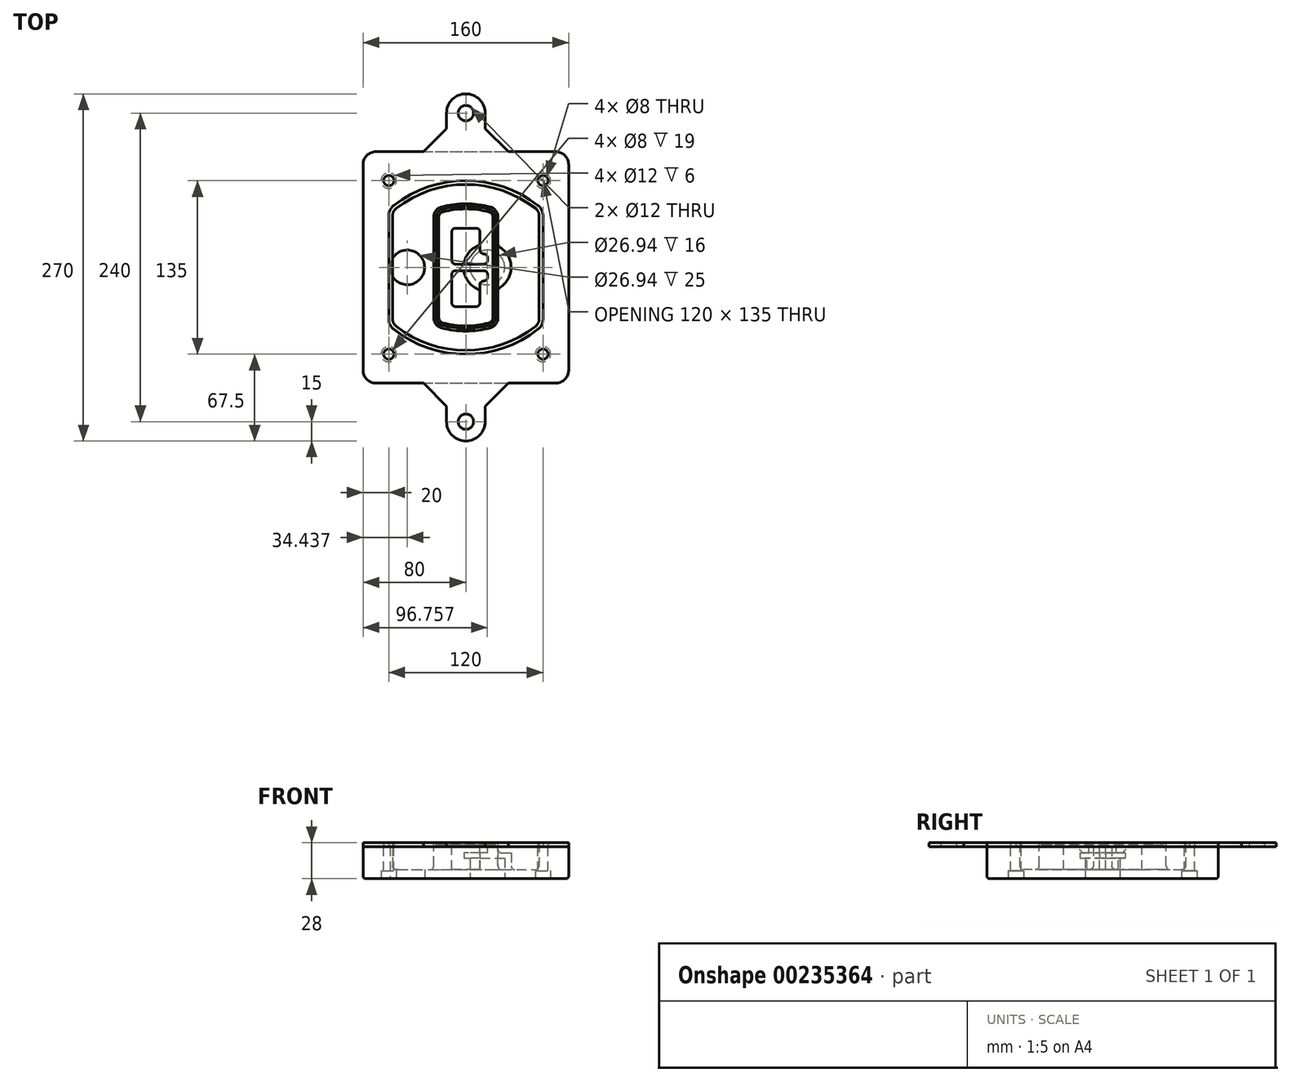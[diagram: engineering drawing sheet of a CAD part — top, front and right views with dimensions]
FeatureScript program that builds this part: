
annotation { "Feature Type Name" : "Feature", "Feature Type Description" : "" }
export const myFeature = defineFeature(function(context is Context, id is Id, definition is map)
    precondition{}
    {
        {
            var Q0;
            Q0=qCreatedBy(makeId("Top.planeOp"),FACE);
            var sketch = newSketch(context, id + "F0", { "sketchPlane" : qUnion([Q0])});
            skPoint(sketch, "E0.rect.middle", {"position": v(0, 0) * mm});
            skLineSegment(sketch, "E1.bottom", {"start": v(-70, -90) * mm, "end": v(70, -90) * mm});
            skLineSegment(sketch, "E1.top", {"start": v(-70, 90) * mm, "end": v(70, 90) * mm});
            skLineSegment(sketch, "E1.left", {"start": v(-80, -80) * mm, "end": v(-80, 80) * mm});
            skLineSegment(sketch, "E1.right", {"start": v(80, -80) * mm, "end": v(80, 80) * mm});
            skLineSegment(sketch, "E2", {"start": v(-80, 90) * mm, "end": v(80, -90) * mm, "construction": true});
            skLineSegment(sketch, "E3", {"start": v(80, 90) * mm, "end": v(-80, -90) * mm, "construction": true});
            skCircle(sketch, "E4", {"center": v(-60, 67.5) * mm, "radius": 4 * mm});
            skCircle(sketch, "E5", {"center": v(60, 67.5) * mm, "radius": 4 * mm});
            skCircle(sketch, "E6", {"center": v(60, -67.5) * mm, "radius": 4 * mm});
            skCircle(sketch, "E7", {"center": v(-60, -67.5) * mm, "radius": 4 * mm});
            skLineSegment(sketch, "E8", {"start": v(-60, 67.5) * mm, "end": v(60, 67.5) * mm, "construction": true});
            skLineSegment(sketch, "E9", {"start": v(60, 67.5) * mm, "end": v(60, -67.5) * mm, "construction": true});
            skLineSegment(sketch, "E10", {"start": v(60, -67.5) * mm, "end": v(-60, -67.5) * mm, "construction": true});
            skLineSegment(sketch, "E11", {"start": v(-60, -67.5) * mm, "end": v(-60, 67.5) * mm, "construction": true});
            skLineSegment(sketch, "E12", {"start": v(-60, 40.3) * mm, "end": v(-60, -40.3) * mm});
            skLineSegment(sketch, "E13", {"start": v(60, 40.3) * mm, "end": v(60, -40.3) * mm});
            skArc(sketch, "E14", {"start": v(56.15, 48.18) * mm, "mid": v(0, 67.5) * mm, "end": v(-56.15, 48.18) * mm});
            skArc(sketch, "E15", {"start": v(-56.15, -48.18) * mm, "mid": v(0, -67.5) * mm, "end": v(56.15, -48.18) * mm});
            skLineSegment(sketch, "E16", {"start": v(-60, 0) * mm, "end": v(60, 0) * mm, "construction": true});
            skPoint(sketch, "E17.visualSharp", {"position": v(-60, -45) * mm});
            skArc(sketch, "E17.filletArc", {"start": v(-60, -40.3) * mm, "mid": v(-58.99, -44.68) * mm, "end": v(-56.15, -48.18) * mm});
            skPoint(sketch, "E18.visualSharp", {"position": v(-60, 45) * mm});
            skArc(sketch, "E18.filletArc", {"start": v(-56.15, 48.18) * mm, "mid": v(-58.99, 44.68) * mm, "end": v(-60, 40.3) * mm});
            skPoint(sketch, "E19.visualSharp", {"position": v(60, 45) * mm});
            skArc(sketch, "E19.filletArc", {"start": v(60, 40.3) * mm, "mid": v(58.99, 44.68) * mm, "end": v(56.15, 48.18) * mm});
            skPoint(sketch, "E20.visualSharp", {"position": v(60, -45) * mm});
            skArc(sketch, "E20.filletArc", {"start": v(56.15, -48.18) * mm, "mid": v(58.99, -44.68) * mm, "end": v(60, -40.3) * mm});
            skPoint(sketch, "E21.visualSharp", {"position": v(-80, 90) * mm});
            skArc(sketch, "E21.filletArc", {"start": v(-70, 90) * mm, "mid": v(-77.07, 87.07) * mm, "end": v(-80, 80) * mm});
            skPoint(sketch, "E22.visualSharp", {"position": v(80, 90) * mm});
            skArc(sketch, "E22.filletArc", {"start": v(80, 80) * mm, "mid": v(77.07, 87.07) * mm, "end": v(70, 90) * mm});
            skPoint(sketch, "E23.visualSharp", {"position": v(80, -90) * mm});
            skArc(sketch, "E23.filletArc", {"start": v(70, -90) * mm, "mid": v(77.07, -87.07) * mm, "end": v(80, -80) * mm});
            skPoint(sketch, "E24.visualSharp", {"position": v(-80, -90) * mm});
            skArc(sketch, "E24.filletArc", {"start": v(-80, -80) * mm, "mid": v(-77.07, -87.07) * mm, "end": v(-70, -90) * mm});
            skArc(sketch, "E25.0", {"start": v(57, 40.3) * mm, "mid": v(56.3, 43.36) * mm, "end": v(54.3, 45.81) * mm});
            skLineSegment(sketch, "E25.1", {"start": v(57, 40.3) * mm, "end": v(57, -40.3) * mm});
            skArc(sketch, "E25.2", {"start": v(54.3, -45.81) * mm, "mid": v(56.3, -43.36) * mm, "end": v(57, -40.3) * mm});
            skArc(sketch, "E25.3", {"start": v(-54.3, -45.81) * mm, "mid": v(0, -64.5) * mm, "end": v(54.3, -45.81) * mm});
            skArc(sketch, "E25.4", {"start": v(-57, -40.3) * mm, "mid": v(-56.3, -43.36) * mm, "end": v(-54.3, -45.81) * mm});
            skArc(sketch, "E25.5", {"start": v(54.3, 45.81) * mm, "mid": v(0, 64.5) * mm, "end": v(-54.3, 45.81) * mm});
            skLineSegment(sketch, "E25.6", {"start": v(-57, 40.3) * mm, "end": v(-57, -40.3) * mm});
            skArc(sketch, "E25.7", {"start": v(-54.3, 45.81) * mm, "mid": v(-56.3, 43.36) * mm, "end": v(-57, 40.3) * mm});
            skArc(sketch, "E26.0", {"start": v(-58.62, 51.33) * mm, "mid": v(-62.58, 46.43) * mm, "end": v(-64, 40.3) * mm});
            skArc(sketch, "E26.1", {"start": v(58.62, 51.33) * mm, "mid": v(0, 71.5) * mm, "end": v(-58.62, 51.33) * mm});
            skArc(sketch, "E26.2", {"start": v(64, 40.3) * mm, "mid": v(62.58, 46.43) * mm, "end": v(58.62, 51.33) * mm});
            skLineSegment(sketch, "E26.3", {"start": v(64, 40.3) * mm, "end": v(64, -40.3) * mm});
            skArc(sketch, "E26.4", {"start": v(58.62, -51.33) * mm, "mid": v(62.58, -46.43) * mm, "end": v(64, -40.3) * mm});
            skLineSegment(sketch, "E26.5", {"start": v(-64, 40.3) * mm, "end": v(-64, -40.3) * mm});
            skArc(sketch, "E26.6", {"start": v(-58.62, -51.33) * mm, "mid": v(0, -71.5) * mm, "end": v(58.62, -51.33) * mm});
            skArc(sketch, "E26.7", {"start": v(-64, -40.3) * mm, "mid": v(-62.58, -46.43) * mm, "end": v(-58.62, -51.33) * mm});
            skSolve(sketch);
        }
        {
            var Q0;
            Q0=makeQuery(id+"F0.imprint","IMPRINT",FACE,{"disambiguationData":[TD([[makeQuery(id+"F0.imprint","IMPRINT",EDGE,{"derivedFrom":sQuery(id+"F0.wireOp",EDGE,"E1.bottom")}),1.0]])]});
            var Q1;
            Q1=makeQuery(id+"F0.imprint","IMPRINT",FACE,{"disambiguationData":[TD([[makeQuery(id+"F0.imprint","IMPRINT",EDGE,{"derivedFrom":sQuery(id+"F0.wireOp",EDGE,"E12")}),1.0]])]});
            var Q2;
            Q2=makeQuery(id+"F0.imprint","IMPRINT",FACE,{"disambiguationData":[TD([[makeQuery(id+"F0.imprint","IMPRINT",EDGE,{"derivedFrom":sQuery(id+"F0.wireOp",EDGE,"E25.0")}),1.0]])]});
            var Q3;
            Q3=makeQuery(id+"F0.imprint","IMPRINT",FACE,{"disambiguationData":[TD([[makeQuery(id+"F0.imprint","IMPRINT",EDGE,{"derivedFrom":sQuery(id+"F0.wireOp",EDGE,"E12")}),-1.0]])]});
            extrude(context, id + "F1", {"entities" : qUnion([Q0, Q1, Q2, Q3]), "oppositeDirection" : true, "depth" : 25 * mm});
        }
        {
            var Q0;
            Q0=makeQuery(id+"F0.imprint","IMPRINT",FACE,{"disambiguationData":[TD([[makeQuery(id+"F0.imprint","IMPRINT",EDGE,{"derivedFrom":sQuery(id+"F0.wireOp",EDGE,"E12")}),1.0]])]});
            extrude(context, id + "F2", {"entities" : qUnion([Q0]), "operationType" : NewBodyOperationType.ADD, "depth" : 3 * mm});
        }
        {
            var Q0;
            Q0=makeQuery(id+"F0.imprint","IMPRINT",FACE,{"disambiguationData":[TD([[makeQuery(id+"F0.imprint","IMPRINT",EDGE,{"derivedFrom":sQuery(id+"F0.wireOp",EDGE,"E25.0")}),1.0]])]});
            extrude(context, id + "F3", {"entities" : qUnion([Q0]), "operationType" : NewBodyOperationType.REMOVE, "oppositeDirection" : true, "depth" : 18 * mm});
        }
        {
            var Q0;
            Q0=makeQuery(id+"F2.opExtrude","CAP_FACE",FACE,{"disambiguationData":[OSD([sQuery(id+"F0.wireOp",EDGE,"E12"),sQuery(id+"F0.wireOp",EDGE,"E13"),sQuery(id+"F0.wireOp",EDGE,"E14"),sQuery(id+"F0.wireOp",EDGE,"E15"),sQuery(id+"F0.wireOp",EDGE,"E17.filletArc"),sQuery(id+"F0.wireOp",EDGE,"E18.filletArc"),sQuery(id+"F0.wireOp",EDGE,"E19.filletArc"),sQuery(id+"F0.wireOp",EDGE,"E20.filletArc"),sQuery(id+"F0.wireOp",EDGE,"E25.0"),sQuery(id+"F0.wireOp",EDGE,"E25.1"),sQuery(id+"F0.wireOp",EDGE,"E25.2"),sQuery(id+"F0.wireOp",EDGE,"E25.3"),sQuery(id+"F0.wireOp",EDGE,"E25.4"),sQuery(id+"F0.wireOp",EDGE,"E25.5"),sQuery(id+"F0.wireOp",EDGE,"E25.6"),sQuery(id+"F0.wireOp",EDGE,"E25.7")])],"isStart":false});
            var sketch = newSketch(context, id + "F4", { "sketchPlane" : qUnion([Q0])});
            skArc(sketch, "E27.0", {"start": v(-19.08, -46.97) * mm, "mid": v(0, -49.5) * mm, "end": v(19.08, -46.97) * mm});
            skArc(sketch, "E28.0", {"start": v(19.08, 46.97) * mm, "mid": v(0, 49.5) * mm, "end": v(-19.08, 46.97) * mm});
            skLineSegment(sketch, "E29", {"start": v(-25, 39.25) * mm, "end": v(-25, -39.25) * mm});
            skLineSegment(sketch, "E30", {"start": v(25, 39.25) * mm, "end": v(25, -39.25) * mm});
            skLineSegment(sketch, "E31", {"start": v(-25, 45.1) * mm, "end": v(25, 45.1) * mm, "construction": true});
            skLineSegment(sketch, "E32", {"start": v(-25, -45.1) * mm, "end": v(25, -45.1) * mm, "construction": true});
            skPoint(sketch, "E33.visualSharp", {"position": v(-25, 45.1) * mm});
            skArc(sketch, "E33.filletArc", {"start": v(-19.08, 46.97) * mm, "mid": v(-23.35, 44.11) * mm, "end": v(-25, 39.25) * mm});
            skPoint(sketch, "E34.visualSharp", {"position": v(25, 45.1) * mm});
            skArc(sketch, "E34.filletArc", {"start": v(25, 39.25) * mm, "mid": v(23.35, 44.11) * mm, "end": v(19.08, 46.97) * mm});
            skPoint(sketch, "E35.visualSharp", {"position": v(25, -45.1) * mm});
            skArc(sketch, "E35.filletArc", {"start": v(19.08, -46.97) * mm, "mid": v(23.35, -44.11) * mm, "end": v(25, -39.25) * mm});
            skPoint(sketch, "E36.visualSharp", {"position": v(-25, -45.1) * mm});
            skArc(sketch, "E36.filletArc", {"start": v(-25, -39.25) * mm, "mid": v(-23.35, -44.11) * mm, "end": v(-19.08, -46.97) * mm});
            skArc(sketch, "E37.0", {"start": v(54.3, 45.81) * mm, "mid": v(0, 64.5) * mm, "end": v(-54.3, 45.81) * mm});
            skArc(sketch, "E37.1", {"start": v(-54.3, 45.81) * mm, "mid": v(-56.3, 43.36) * mm, "end": v(-57, 40.3) * mm});
            skLineSegment(sketch, "E37.2", {"start": v(-57, 40.3) * mm, "end": v(-57, -40.3) * mm});
            skArc(sketch, "E37.3", {"start": v(-57, -40.3) * mm, "mid": v(-56.3, -43.36) * mm, "end": v(-54.3, -45.81) * mm});
            skArc(sketch, "E37.4", {"start": v(-54.3, -45.81) * mm, "mid": v(0, -64.5) * mm, "end": v(54.3, -45.81) * mm});
            skArc(sketch, "E37.5", {"start": v(54.3, -45.81) * mm, "mid": v(56.3, -43.36) * mm, "end": v(57, -40.3) * mm});
            skLineSegment(sketch, "E37.6", {"start": v(57, 40.3) * mm, "end": v(57, -40.3) * mm});
            skArc(sketch, "E37.7", {"start": v(57, 40.3) * mm, "mid": v(56.3, 43.36) * mm, "end": v(54.3, 45.81) * mm});
            skLineSegment(sketch, "E38.0", {"start": v(23, 39.25) * mm, "end": v(23, -39.25) * mm});
            skArc(sketch, "E38.1", {"start": v(18.56, -45.04) * mm, "mid": v(21.76, -42.9) * mm, "end": v(23, -39.25) * mm});
            skArc(sketch, "E38.2", {"start": v(-18.56, -45.04) * mm, "mid": v(0, -47.5) * mm, "end": v(18.56, -45.04) * mm});
            skArc(sketch, "E38.3", {"start": v(-23, -39.25) * mm, "mid": v(-21.76, -42.9) * mm, "end": v(-18.56, -45.04) * mm});
            skLineSegment(sketch, "E38.4", {"start": v(-23, 39.25) * mm, "end": v(-23, -39.25) * mm});
            skArc(sketch, "E38.5", {"start": v(23, 39.25) * mm, "mid": v(21.76, 42.9) * mm, "end": v(18.56, 45.04) * mm});
            skArc(sketch, "E38.6", {"start": v(-18.56, 45.04) * mm, "mid": v(-21.76, 42.9) * mm, "end": v(-23, 39.25) * mm});
            skArc(sketch, "E38.7", {"start": v(18.56, 45.04) * mm, "mid": v(0, 47.5) * mm, "end": v(-18.56, 45.04) * mm});
            skArc(sketch, "E39.0", {"start": v(21, 39.25) * mm, "mid": v(20.18, 41.68) * mm, "end": v(18.04, 43.1) * mm});
            skLineSegment(sketch, "E39.1", {"start": v(21, 39.25) * mm, "end": v(21, -39.25) * mm});
            skArc(sketch, "E39.2", {"start": v(18.04, -43.1) * mm, "mid": v(20.18, -41.68) * mm, "end": v(21, -39.25) * mm});
            skArc(sketch, "E39.3", {"start": v(-18.04, -43.1) * mm, "mid": v(0, -45.5) * mm, "end": v(18.04, -43.1) * mm});
            skArc(sketch, "E39.4", {"start": v(-21, -39.25) * mm, "mid": v(-20.18, -41.68) * mm, "end": v(-18.04, -43.1) * mm});
            skArc(sketch, "E39.5", {"start": v(18.04, 43.1) * mm, "mid": v(0, 45.5) * mm, "end": v(-18.04, 43.1) * mm});
            skLineSegment(sketch, "E39.6", {"start": v(-21, 39.25) * mm, "end": v(-21, -39.25) * mm});
            skArc(sketch, "E39.7", {"start": v(-18.04, 43.1) * mm, "mid": v(-20.18, 41.68) * mm, "end": v(-21, 39.25) * mm});
            skLineSegment(sketch, "E40", {"start": v(-25, 0) * mm, "end": v(25, 0) * mm, "construction": true});
            skLineSegment(sketch, "E41", {"start": v(-11, 5.5) * mm, "end": v(-11, 27.5) * mm});
            skLineSegment(sketch, "E42", {"start": v(-8, 30.5) * mm, "end": v(8, 30.5) * mm});
            skLineSegment(sketch, "E43", {"start": v(11, 27.5) * mm, "end": v(11, 13.5) * mm});
            skLineSegment(sketch, "E44", {"start": v(14, 10.5) * mm, "end": v(14, 10.5) * mm});
            skLineSegment(sketch, "E45", {"start": v(17, 7.5) * mm, "end": v(17, 5.5) * mm});
            skLineSegment(sketch, "E46", {"start": v(14, 2.5) * mm, "end": v(-8, 2.5) * mm});
            skPoint(sketch, "E47.visualSharp", {"position": v(-11, 30.5) * mm});
            skArc(sketch, "E47.filletArc", {"start": v(-8, 30.5) * mm, "mid": v(-10.12, 29.62) * mm, "end": v(-11, 27.5) * mm});
            skPoint(sketch, "E48.visualSharp", {"position": v(11, 30.5) * mm});
            skArc(sketch, "E48.filletArc", {"start": v(11, 27.5) * mm, "mid": v(10.12, 29.62) * mm, "end": v(8, 30.5) * mm});
            skPoint(sketch, "E49.visualSharp", {"position": v(11, 10.5) * mm});
            skArc(sketch, "E49.filletArc", {"start": v(11, 13.5) * mm, "mid": v(11.88, 11.38) * mm, "end": v(14, 10.5) * mm});
            skPoint(sketch, "E50.visualSharp", {"position": v(17, 10.5) * mm});
            skArc(sketch, "E50.filletArc", {"start": v(17, 7.5) * mm, "mid": v(16.12, 9.62) * mm, "end": v(14, 10.5) * mm});
            skPoint(sketch, "E51.visualSharp", {"position": v(17, 2.5) * mm});
            skArc(sketch, "E51.filletArc", {"start": v(14, 2.5) * mm, "mid": v(16.12, 3.38) * mm, "end": v(17, 5.5) * mm});
            skPoint(sketch, "E52.visualSharp", {"position": v(-11, 2.5) * mm});
            skArc(sketch, "E52.filletArc", {"start": v(-11, 5.5) * mm, "mid": v(-10.12, 3.38) * mm, "end": v(-8, 2.5) * mm});
            skLineSegment(sketch, "E53.0.MirrorCS", {"start": v(14, -2.5) * mm, "end": v(-8, -2.5) * mm});
            skArc(sketch, "E54.0.MirrorCS", {"start": v(-11, -5.5) * mm, "mid": v(-10.12, -3.38) * mm, "end": v(-8, -2.5) * mm});
            skLineSegment(sketch, "E55.0.MirrorCS", {"start": v(-11, -5.5) * mm, "end": v(-11, -27.5) * mm});
            skArc(sketch, "E56.0.MirrorCS", {"start": v(-8, -30.5) * mm, "mid": v(-10.12, -29.62) * mm, "end": v(-11, -27.5) * mm});
            skLineSegment(sketch, "E57.0.MirrorCS", {"start": v(-8, -30.5) * mm, "end": v(8, -30.5) * mm});
            skArc(sketch, "E58.0.MirrorCS", {"start": v(11, -27.5) * mm, "mid": v(10.12, -29.62) * mm, "end": v(8, -30.5) * mm});
            skLineSegment(sketch, "E59.0.MirrorCS", {"start": v(11, -27.5) * mm, "end": v(11, -13.5) * mm});
            skArc(sketch, "E60.0.MirrorCS", {"start": v(11, -13.5) * mm, "mid": v(11.88, -11.38) * mm, "end": v(14, -10.5) * mm});
            skArc(sketch, "E61.0.MirrorCS", {"start": v(17, -7.5) * mm, "mid": v(16.12, -9.62) * mm, "end": v(14, -10.5) * mm});
            skLineSegment(sketch, "E62.0.MirrorCS", {"start": v(17, -7.5) * mm, "end": v(17, -5.5) * mm});
            skArc(sketch, "E63.0.MirrorCS", {"start": v(14, -2.5) * mm, "mid": v(16.12, -3.38) * mm, "end": v(17, -5.5) * mm});
            skSolve(sketch);
        }
        {
            var Q0;
            Q0=makeQuery(id+"F4.imprint","IMPRINT",FACE,{"disambiguationData":[TD([[makeQuery(id+"F4.imprint","IMPRINT",EDGE,{"derivedFrom":sQuery(id+"F4.wireOp",EDGE,"E27.0")}),1.0]])]});
            var Q1;
            Q1=makeQuery(id+"F4.imprint","IMPRINT",FACE,{"disambiguationData":[TD([[makeQuery(id+"F4.imprint","IMPRINT",EDGE,{"derivedFrom":sQuery(id+"F4.wireOp",EDGE,"E38.0")}),-1.0]])]});
            var Q2;
            Q2=makeQuery(id+"F4.imprint","IMPRINT",FACE,{"disambiguationData":[TD([[makeQuery(id+"F4.imprint","IMPRINT",EDGE,{"derivedFrom":sQuery(id+"F4.wireOp",EDGE,"E39.0")}),1.0]])]});
            extrude(context, id + "F5", {"entities" : qUnion([Q0, Q1, Q2]), "operationType" : NewBodyOperationType.ADD, "endBound" : BoundingType.UP_TO_NEXT, "oppositeDirection" : true, "depth" : 25 * mm});
        }
        {
            var Q0;
            Q0=makeQuery(id+"F4.imprint","IMPRINT",FACE,{"disambiguationData":[TD([[makeQuery(id+"F4.imprint","IMPRINT",EDGE,{"derivedFrom":sQuery(id+"F4.wireOp",EDGE,"E38.0")}),-1.0]])]});
            extrude(context, id + "F6", {"entities" : qUnion([Q0]), "operationType" : NewBodyOperationType.REMOVE, "oppositeDirection" : true, "depth" : 2 * mm});
        }
        {
            var Q0;
            Q0=makeQuery(id+"F1.opExtrude","CAP_FACE",FACE,{"disambiguationData":[OSD([sQuery(id+"F0.wireOp",EDGE,"E1.bottom"),sQuery(id+"F0.wireOp",EDGE,"E1.top"),sQuery(id+"F0.wireOp",EDGE,"E1.left"),sQuery(id+"F0.wireOp",EDGE,"E1.right"),sQuery(id+"F0.wireOp",EDGE,"E4"),sQuery(id+"F0.wireOp",EDGE,"E5"),sQuery(id+"F0.wireOp",EDGE,"E6"),sQuery(id+"F0.wireOp",EDGE,"E7"),sQuery(id+"F0.wireOp",EDGE,"E21.filletArc"),sQuery(id+"F0.wireOp",EDGE,"E22.filletArc"),sQuery(id+"F0.wireOp",EDGE,"E23.filletArc"),sQuery(id+"F0.wireOp",EDGE,"E24.filletArc")])],"isStart":false});
            var sketch = newSketch(context, id + "F7", { "sketchPlane" : qUnion([Q0])});
            skCircle(sketch, "E64", {"center": v(16.76, 0) * mm, "radius": 13.47 * mm});
            skCircle(sketch, "E65", {"center": v(-45.56, 0) * mm, "radius": 13.47 * mm});
            skLineSegment(sketch, "E66", {"start": v(80, 0) * mm, "end": v(-80, 0) * mm});
            skCircle(sketch, "E67", {"center": v(16.76, 0) * mm, "radius": 18.47 * mm});
            skCircle(sketch, "E68", {"center": v(60, -67.5) * mm, "radius": 6 * mm});
            skCircle(sketch, "E69", {"center": v(-60, -67.5) * mm, "radius": 6 * mm});
            skCircle(sketch, "E70", {"center": v(-60, 67.5) * mm, "radius": 6 * mm});
            skCircle(sketch, "E71", {"center": v(60, 67.5) * mm, "radius": 6 * mm});
            skSolve(sketch);
        }
        {
            var Q0;
            {var subQ1=sQuery(id+"F7.wireOp",EDGE,"E66");var subQ4=sQuery(id+"F7.wireOp",EDGE,"E64");var subQ6=makeQuery(id+"F7.imprint","INTERSECT",VERTEX,{"disambiguationData":[OD(0.0)],"derivedFrom":[subQ4,subQ1]});Q0=makeQuery(id+"F7.imprint","IMPRINT",FACE,{"disambiguationData":[TD([[makeQuery(id+"F7.imprint","IMPRINT",EDGE,{"disambiguationData":[TD([[subQ6,-1.0]])],"derivedFrom":subQ4}),-1.0]])]});}
            var Q1;
            {var subQ0=sQuery(id+"F7.wireOp",EDGE,"E66");var subQ1=sQuery(id+"F7.wireOp",EDGE,"E64");var subQ3=makeQuery(id+"F7.imprint","INTERSECT",VERTEX,{"disambiguationData":[OD(0.0)],"derivedFrom":[subQ1,subQ0]});Q1=makeQuery(id+"F7.imprint","IMPRINT",FACE,{"disambiguationData":[TD([[makeQuery(id+"F7.imprint","IMPRINT",EDGE,{"disambiguationData":[TD([[subQ3,-1.0]])],"derivedFrom":subQ1}),1.0]])]});}
            var Q2;
            {var subQ0=sQuery(id+"F7.wireOp",EDGE,"E66");var subQ1=sQuery(id+"F7.wireOp",EDGE,"E64");var subQ3=makeQuery(id+"F7.imprint","INTERSECT",VERTEX,{"disambiguationData":[OD(0.0)],"derivedFrom":[subQ1,subQ0]});Q2=makeQuery(id+"F7.imprint","IMPRINT",FACE,{"disambiguationData":[TD([[makeQuery(id+"F7.imprint","IMPRINT",EDGE,{"disambiguationData":[TD([[subQ3,1.0]])],"derivedFrom":subQ1}),1.0]])]});}
            var Q3;
            {var subQ1=sQuery(id+"F7.wireOp",EDGE,"E66");var subQ4=sQuery(id+"F7.wireOp",EDGE,"E64");var subQ6=makeQuery(id+"F7.imprint","INTERSECT",VERTEX,{"disambiguationData":[OD(0.0)],"derivedFrom":[subQ4,subQ1]});Q3=makeQuery(id+"F7.imprint","IMPRINT",FACE,{"disambiguationData":[TD([[makeQuery(id+"F7.imprint","IMPRINT",EDGE,{"disambiguationData":[TD([[subQ6,1.0]])],"derivedFrom":subQ4}),-1.0]])]});}
            extrude(context, id + "F8", {"entities" : qUnion([Q0, Q1, Q2, Q3]), "operationType" : NewBodyOperationType.ADD, "oppositeDirection" : true, "depth" : 20 * mm});
        }
        {
            var Q0;
            {var subQ0=sQuery(id+"F7.wireOp",EDGE,"E66");var subQ1=sQuery(id+"F7.wireOp",EDGE,"E64");var subQ3=makeQuery(id+"F7.imprint","INTERSECT",VERTEX,{"disambiguationData":[OD(0.0)],"derivedFrom":[subQ1,subQ0]});Q0=makeQuery(id+"F7.imprint","IMPRINT",FACE,{"disambiguationData":[TD([[makeQuery(id+"F7.imprint","IMPRINT",EDGE,{"disambiguationData":[TD([[subQ3,-1.0]])],"derivedFrom":subQ1}),1.0]])]});}
            var Q1;
            {var subQ0=sQuery(id+"F7.wireOp",EDGE,"E66");var subQ1=sQuery(id+"F7.wireOp",EDGE,"E64");var subQ3=makeQuery(id+"F7.imprint","INTERSECT",VERTEX,{"disambiguationData":[OD(0.0)],"derivedFrom":[subQ1,subQ0]});Q1=makeQuery(id+"F7.imprint","IMPRINT",FACE,{"disambiguationData":[TD([[makeQuery(id+"F7.imprint","IMPRINT",EDGE,{"disambiguationData":[TD([[subQ3,1.0]])],"derivedFrom":subQ1}),1.0]])]});}
            extrude(context, id + "F9", {"entities" : qUnion([Q0, Q1]), "operationType" : NewBodyOperationType.REMOVE, "oppositeDirection" : true, "depth" : 16 * mm});
        }
        {
            var Q0;
            {var subQ0=sQuery(id+"F7.wireOp",EDGE,"E66");var subQ1=sQuery(id+"F7.wireOp",EDGE,"E65");var subQ3=makeQuery(id+"F7.imprint","INTERSECT",VERTEX,{"disambiguationData":[OD(0.0)],"derivedFrom":[subQ1,subQ0]});Q0=makeQuery(id+"F7.imprint","IMPRINT",FACE,{"disambiguationData":[TD([[makeQuery(id+"F7.imprint","IMPRINT",EDGE,{"disambiguationData":[TD([[subQ3,-1.0]])],"derivedFrom":subQ1}),1.0]])]});}
            var Q1;
            {var subQ0=sQuery(id+"F7.wireOp",EDGE,"E66");var subQ1=sQuery(id+"F7.wireOp",EDGE,"E65");var subQ3=makeQuery(id+"F7.imprint","INTERSECT",VERTEX,{"disambiguationData":[OD(0.0)],"derivedFrom":[subQ1,subQ0]});Q1=makeQuery(id+"F7.imprint","IMPRINT",FACE,{"disambiguationData":[TD([[makeQuery(id+"F7.imprint","IMPRINT",EDGE,{"disambiguationData":[TD([[subQ3,1.0]])],"derivedFrom":subQ1}),1.0]])]});}
            extrude(context, id + "F10", {"entities" : qUnion([Q0, Q1]), "operationType" : NewBodyOperationType.REMOVE, "oppositeDirection" : true, "depth" : 25 * mm});
        }
        {
            var Q0;
            Q0=makeQuery(id+"F7.imprint","IMPRINT",FACE,{"disambiguationData":[TD([[makeQuery(id+"F7.imprint","IMPRINT",EDGE,{"derivedFrom":sQuery(id+"F7.wireOp",EDGE,"E68")}),1.0]])]});
            var Q1;
            Q1=makeQuery(id+"F7.imprint","IMPRINT",FACE,{"disambiguationData":[TD([[makeQuery(id+"F7.imprint","IMPRINT",EDGE,{"derivedFrom":makeQuery(id+"F1.opExtrude","CAP_EDGE",EDGE,{"disambiguationData":[OSD([sQuery(id+"F0.wireOp",EDGE,"E5")])],"isStart":false})}),-1.0]])]});
            var Q2;
            Q2=makeQuery(id+"F7.imprint","IMPRINT",FACE,{"disambiguationData":[TD([[makeQuery(id+"F7.imprint","IMPRINT",EDGE,{"derivedFrom":sQuery(id+"F7.wireOp",EDGE,"E69")}),1.0]])]});
            var Q3;
            Q3=makeQuery(id+"F7.imprint","IMPRINT",FACE,{"disambiguationData":[TD([[makeQuery(id+"F7.imprint","IMPRINT",EDGE,{"derivedFrom":makeQuery(id+"F1.opExtrude","CAP_EDGE",EDGE,{"disambiguationData":[OSD([sQuery(id+"F0.wireOp",EDGE,"E4")])],"isStart":false})}),-1.0]])]});
            var Q4;
            Q4=makeQuery(id+"F7.imprint","IMPRINT",FACE,{"disambiguationData":[TD([[makeQuery(id+"F7.imprint","IMPRINT",EDGE,{"derivedFrom":sQuery(id+"F7.wireOp",EDGE,"E70")}),1.0]])]});
            var Q5;
            Q5=makeQuery(id+"F7.imprint","IMPRINT",FACE,{"disambiguationData":[TD([[makeQuery(id+"F7.imprint","IMPRINT",EDGE,{"derivedFrom":makeQuery(id+"F1.opExtrude","CAP_EDGE",EDGE,{"disambiguationData":[OSD([sQuery(id+"F0.wireOp",EDGE,"E7")])],"isStart":false})}),-1.0]])]});
            var Q6;
            Q6=makeQuery(id+"F7.imprint","IMPRINT",FACE,{"disambiguationData":[TD([[makeQuery(id+"F7.imprint","IMPRINT",EDGE,{"derivedFrom":sQuery(id+"F7.wireOp",EDGE,"E71")}),1.0]])]});
            var Q7;
            Q7=makeQuery(id+"F7.imprint","IMPRINT",FACE,{"disambiguationData":[TD([[makeQuery(id+"F7.imprint","IMPRINT",EDGE,{"derivedFrom":makeQuery(id+"F1.opExtrude","CAP_EDGE",EDGE,{"disambiguationData":[OSD([sQuery(id+"F0.wireOp",EDGE,"E6")])],"isStart":false})}),-1.0]])]});
            extrude(context, id + "F11", {"entities" : qUnion([Q0, Q1, Q2, Q3, Q4, Q5, Q6, Q7]), "operationType" : NewBodyOperationType.REMOVE, "oppositeDirection" : true, "depth" : 6 * mm});
        }
        {
            var Q0;
            Q0=makeQuery(id+"F9.boolean.opBoolean","COPY",FACE,{"derivedFrom":makeQuery(id+"F9.opExtrude","CAP_FACE",FACE,{"disambiguationData":[OSD([sQuery(id+"F7.wireOp",EDGE,"E64")])],"isStart":false})});
            var sketch = newSketch(context, id + "F12", { "sketchPlane" : qUnion([Q0])});
            skArc(sketch, "E72.0", {"start": v(11, 17.55) * mm, "mid": v(2.57, 11.82) * mm, "end": v(-1.54, 2.5) * mm});
            skArc(sketch, "E72.1", {"start": v(-1.54, -2.5) * mm, "mid": v(2.57, -11.82) * mm, "end": v(11, -17.55) * mm});
            skLineSegment(sketch, "E73", {"start": v(-1.54, -2.5) * mm, "end": v(14, -2.5) * mm});
            skLineSegment(sketch, "E74.0", {"start": v(14, 2.5) * mm, "end": v(-1.54, 2.5) * mm});
            skArc(sketch, "E74.1", {"start": v(14, 2.5) * mm, "mid": v(16.12, 3.38) * mm, "end": v(17, 5.5) * mm});
            skLineSegment(sketch, "E74.2", {"start": v(17, 7.5) * mm, "end": v(17, 5.5) * mm});
            skArc(sketch, "E74.3", {"start": v(17, 7.5) * mm, "mid": v(16.12, 9.62) * mm, "end": v(14, 10.5) * mm});
            skArc(sketch, "E74.4", {"start": v(11, 13.5) * mm, "mid": v(11.88, 11.38) * mm, "end": v(14, 10.5) * mm});
            skLineSegment(sketch, "E74.5", {"start": v(11, 17.55) * mm, "end": v(11, 13.5) * mm});
            skLineSegment(sketch, "E74.7", {"start": v(14, -2.5) * mm, "end": v(-1.54, -2.5) * mm});
            skArc(sketch, "E74.8", {"start": v(14, -2.5) * mm, "mid": v(16.12, -3.38) * mm, "end": v(17, -5.5) * mm});
            skLineSegment(sketch, "E74.9", {"start": v(17, -7.5) * mm, "end": v(17, -5.5) * mm});
            skArc(sketch, "E74.10", {"start": v(17, -7.5) * mm, "mid": v(16.12, -9.62) * mm, "end": v(14, -10.5) * mm});
            skArc(sketch, "E74.11", {"start": v(11, -13.5) * mm, "mid": v(11.88, -11.38) * mm, "end": v(14, -10.5) * mm});
            skLineSegment(sketch, "E74.12", {"start": v(11, -17.55) * mm, "end": v(11, -13.5) * mm});
            skPoint(sketch, "E75.orphan", {"position": v(11, -27.5) * mm});
            skPoint(sketch, "E76.orphan", {"position": v(-8, -2.5) * mm});
            skPoint(sketch, "E77.orphan", {"position": v(-8, 2.5) * mm});
            skPoint(sketch, "E78.orphan", {"position": v(11, 27.5) * mm});
            skSolve(sketch);
        }
        {
            var Q0;
            {var subQ7=sQuery(id+"F12.wireOp",EDGE,"E72.0");var subQ14=sQuery(id+"F12.wireOp",EDGE,"E72.1");var subQ16=sQuery(id+"F12.wireOp",EDGE,"E74.1");var subQ18=sQuery(id+"F12.wireOp",EDGE,"E74.8");Q0=qUnion([makeQuery(id+"F12.imprint","IMPRINT",FACE,{"disambiguationData":[TD([[makeQuery(id+"F12.imprint","IMPRINT",EDGE,{"derivedFrom":subQ7}),1.0]])]}),makeQuery(id+"F12.imprint","IMPRINT",FACE,{"disambiguationData":[TD([[makeQuery(id+"F12.imprint","IMPRINT",EDGE,{"derivedFrom":subQ14}),1.0]])]}),makeQuery(id+"F12.imprint","IMPRINT",FACE,{"disambiguationData":[TD([[makeQuery(id+"F12.imprint","IMPRINT",EDGE,{"derivedFrom":subQ16}),1.0]])]}),makeQuery(id+"F12.imprint","IMPRINT",FACE,{"disambiguationData":[TD([[makeQuery(id+"F12.imprint","IMPRINT",EDGE,{"derivedFrom":subQ18}),-1.0]])]})]);}
            var Q1;
            Q1=makeQuery(id+"F5.boolean.opBoolean","SPLIT",FACE,{"disambiguationData":[TD([makeQuery(id+"F5.opExtrude","SWEPT_FACE",FACE,{"disambiguationData":[OSD([sQuery(id+"F4.wireOp",EDGE,"E41")])]})])],"derivedFrom":makeQuery(id+"F3.boolean.opBoolean","COPY",FACE,{"derivedFrom":makeQuery(id+"F3.opExtrude","CAP_FACE",FACE,{"disambiguationData":[OSD([sQuery(id+"F0.wireOp",EDGE,"E25.0"),sQuery(id+"F0.wireOp",EDGE,"E25.1"),sQuery(id+"F0.wireOp",EDGE,"E25.2"),sQuery(id+"F0.wireOp",EDGE,"E25.3"),sQuery(id+"F0.wireOp",EDGE,"E25.4"),sQuery(id+"F0.wireOp",EDGE,"E25.5"),sQuery(id+"F0.wireOp",EDGE,"E25.6"),sQuery(id+"F0.wireOp",EDGE,"E25.7")])],"isStart":false})})});
            extrude(context, id + "F13", {"entities" : qUnion([Q0]), "operationType" : NewBodyOperationType.REMOVE, "endBound" : BoundingType.UP_TO_SURFACE, "endBoundEntityFace" : qUnion([Q1]), "depth" : 25 * mm});
        }
        {
            var Q0;
            Q0=makeQuery(id+"F3.boolean.opBoolean","COPY",EDGE,{"derivedFrom":makeQuery(id+"F3.opExtrude","CAP_EDGE",EDGE,{"disambiguationData":[OSD([sQuery(id+"F0.wireOp",EDGE,"E25.6")])],"isStart":false})});
            var Q1;
            Q1=makeQuery(id+"F8.boolean.opBoolean","INTERSECT",EDGE,{"derivedFrom":[makeQuery(id+"F5.opExtrude","SWEPT_FACE",FACE,{"disambiguationData":[OSD([sQuery(id+"F4.wireOp",EDGE,"E30")])]}),makeQuery(id+"F8.opExtrude","CAP_FACE",FACE,{"disambiguationData":[OSD([sQuery(id+"F7.wireOp",EDGE,"E67")])],"isStart":false})]});
            var Q2;
            Q2=makeQuery(id+"F8.boolean.opBoolean","INTERSECT",EDGE,{"disambiguationData":[OD(1.0)],"derivedFrom":[makeQuery(id+"F5.opExtrude","SWEPT_FACE",FACE,{"disambiguationData":[OSD([sQuery(id+"F4.wireOp",EDGE,"E30")])]}),makeQuery(id+"F8.opExtrude","SWEPT_FACE",FACE,{"disambiguationData":[OSD([sQuery(id+"F7.wireOp",EDGE,"E67")])]})]});
            var Q3;
            {var subQ0=sQuery(id+"F4.wireOp",EDGE,"E30");Q3=makeQuery(id+"F8.boolean.opBoolean","SPLIT",EDGE,{"disambiguationData":[TD([makeQuery(id+"F5.opExtrude","SWEPT_FACE",FACE,{"disambiguationData":[OSD([sQuery(id+"F4.wireOp",EDGE,"E35.filletArc")])]})])],"derivedFrom":makeQuery(id+"F5.opExtrude","CAP_EDGE",EDGE,{"disambiguationData":[OSD([subQ0])],"isStart":false})});}
            var Q4;
            {var subQ0=sQuery(id+"F0.wireOp",EDGE,"E25.7");var subQ1=sQuery(id+"F0.wireOp",EDGE,"E25.1");var subQ2=sQuery(id+"F0.wireOp",EDGE,"E25.6");var subQ3=sQuery(id+"F0.wireOp",EDGE,"E25.5");var subQ4=sQuery(id+"F0.wireOp",EDGE,"E25.4");var subQ5=sQuery(id+"F0.wireOp",EDGE,"E25.0");var subQ6=sQuery(id+"F0.wireOp",EDGE,"E25.2");var subQ7=sQuery(id+"F0.wireOp",EDGE,"E25.3");Q4=makeQuery(id+"F8.boolean.opBoolean","INTERSECT",EDGE,{"derivedFrom":[makeQuery(id+"F5.boolean.opBoolean","SPLIT",FACE,{"disambiguationData":[TD([makeQuery(id+"F2.opExtrude","SWEPT_FACE",FACE,{"disambiguationData":[OSD([subQ5])]})])],"derivedFrom":makeQuery(id+"F3.boolean.opBoolean","COPY",FACE,{"derivedFrom":makeQuery(id+"F3.opExtrude","CAP_FACE",FACE,{"disambiguationData":[OSD([subQ5,subQ1,subQ6,subQ7,subQ4,subQ3,subQ2,subQ0])],"isStart":false})})}),makeQuery(id+"F8.opExtrude","SWEPT_FACE",FACE,{"disambiguationData":[OSD([sQuery(id+"F7.wireOp",EDGE,"E67")])]})]});}
            var Q5;
            Q5=makeQuery(id+"F8.boolean.opBoolean","INTERSECT",EDGE,{"disambiguationData":[OD(0.0)],"derivedFrom":[makeQuery(id+"F5.opExtrude","SWEPT_FACE",FACE,{"disambiguationData":[OSD([sQuery(id+"F4.wireOp",EDGE,"E30")])]}),makeQuery(id+"F8.opExtrude","SWEPT_FACE",FACE,{"disambiguationData":[OSD([sQuery(id+"F7.wireOp",EDGE,"E67")])]})]});
            fillet(context, id + "F14", {"entities" : qUnion([Q0, Q1, Q2, Q3, Q4, Q5]), "radius" : 3 * mm, "tangentPropagation" : true, "allowEdgeOverflow" : false});
        }
        {
            var Q0;
            Q0=makeQuery(id+"F1.opExtrude","CAP_EDGE",EDGE,{"disambiguationData":[OSD([sQuery(id+"F0.wireOp",EDGE,"E1.bottom")])],"isStart":false});
            fillet(context, id + "F15", {"entities" : qUnion([Q0]), "radius" : 2 * mm, "tangentPropagation" : true, "allowEdgeOverflow" : false});
        }
        {
            var Q0;
            {var subQ0=sQuery(id+"F0.wireOp",EDGE,"E22.filletArc");var subQ1=sQuery(id+"F0.wireOp",EDGE,"E7");var subQ2=sQuery(id+"F0.wireOp",EDGE,"E6");var subQ3=sQuery(id+"F0.wireOp",EDGE,"E5");var subQ4=sQuery(id+"F0.wireOp",EDGE,"E4");var subQ5=sQuery(id+"F0.wireOp",EDGE,"E1.bottom");var subQ6=sQuery(id+"F0.wireOp",EDGE,"E21.filletArc");var subQ7=sQuery(id+"F0.wireOp",EDGE,"E1.top");var subQ8=sQuery(id+"F0.wireOp",EDGE,"E1.left");var subQ9=sQuery(id+"F0.wireOp",EDGE,"E1.right");var subQ10=sQuery(id+"F0.wireOp",EDGE,"E23.filletArc");var subQ11=sQuery(id+"F0.wireOp",EDGE,"E24.filletArc");Q0=makeQuery(id+"F2.boolean.opBoolean","SPLIT",FACE,{"disambiguationData":[TD([makeQuery(id+"F1.opExtrude","SWEPT_FACE",FACE,{"disambiguationData":[OSD([subQ5])]})])],"derivedFrom":makeQuery(id+"F1.opExtrude","CAP_FACE",FACE,{"disambiguationData":[OSD([subQ5,subQ7,subQ8,subQ9,subQ4,subQ3,subQ2,subQ1,subQ6,subQ0,subQ10,subQ11])],"isStart":true})});}
            var sketch = newSketch(context, id + "F16", { "sketchPlane" : qUnion([Q0])});
            skLineSegment(sketch, "E79.0", {"start": v(60, 40.3) * mm, "end": v(60, -40.3) * mm});
            skArc(sketch, "E79.1", {"start": v(60, 40.3) * mm, "mid": v(58.99, 44.68) * mm, "end": v(56.15, 48.18) * mm});
            skArc(sketch, "E79.2", {"start": v(56.15, 48.18) * mm, "mid": v(0, 67.5) * mm, "end": v(-56.15, 48.18) * mm});
            skArc(sketch, "E79.3", {"start": v(-56.15, 48.18) * mm, "mid": v(-58.99, 44.68) * mm, "end": v(-60, 40.3) * mm});
            skLineSegment(sketch, "E79.4", {"start": v(-60, 40.3) * mm, "end": v(-60, -40.3) * mm});
            skArc(sketch, "E79.5", {"start": v(-60, -40.3) * mm, "mid": v(-58.99, -44.68) * mm, "end": v(-56.15, -48.18) * mm});
            skArc(sketch, "E79.6", {"start": v(-56.15, -48.18) * mm, "mid": v(0, -67.5) * mm, "end": v(56.15, -48.18) * mm});
            skArc(sketch, "E79.7", {"start": v(56.15, -48.18) * mm, "mid": v(58.99, -44.68) * mm, "end": v(60, -40.3) * mm});
            skCircle(sketch, "E79.8", {"center": v(-60, 67.5) * mm, "radius": 4 * mm});
            skCircle(sketch, "E79.9", {"center": v(60, 67.5) * mm, "radius": 4 * mm});
            skCircle(sketch, "E79.10", {"center": v(60, -67.5) * mm, "radius": 4 * mm});
            skCircle(sketch, "E79.11", {"center": v(-60, -67.5) * mm, "radius": 4 * mm});
            skLineSegment(sketch, "E79.12", {"start": v(-80, -80) * mm, "end": v(-80, 80) * mm});
            skArc(sketch, "E79.13", {"start": v(-70, 90) * mm, "mid": v(-77.07, 87.07) * mm, "end": v(-80, 80) * mm});
            skLineSegment(sketch, "E79.14", {"start": v(-70, 90) * mm, "end": v(70, 90) * mm});
            skArc(sketch, "E79.15", {"start": v(80, 80) * mm, "mid": v(77.07, 87.07) * mm, "end": v(70, 90) * mm});
            skLineSegment(sketch, "E79.16", {"start": v(80, -80) * mm, "end": v(80, 80) * mm});
            skArc(sketch, "E79.17", {"start": v(70, -90) * mm, "mid": v(77.07, -87.07) * mm, "end": v(80, -80) * mm});
            skLineSegment(sketch, "E79.18", {"start": v(-70, -90) * mm, "end": v(70, -90) * mm});
            skArc(sketch, "E79.19", {"start": v(-80, -80) * mm, "mid": v(-77.07, -87.07) * mm, "end": v(-70, -90) * mm});
            skLineSegment(sketch, "E80", {"start": v(0, 90) * mm, "end": v(0, 120) * mm, "construction": true});
            skCircle(sketch, "E81", {"center": v(0, 120) * mm, "radius": 6 * mm});
            skLineSegment(sketch, "E82", {"start": v(-33, 90) * mm, "end": v(-15, 108) * mm});
            skLineSegment(sketch, "E83", {"start": v(-15, 108) * mm, "end": v(-15, 120) * mm});
            skLineSegment(sketch, "E84", {"start": v(33, 90) * mm, "end": v(15, 108) * mm});
            skLineSegment(sketch, "E85", {"start": v(15, 108) * mm, "end": v(15, 120) * mm});
            skArc(sketch, "E86", {"start": v(15, 120) * mm, "mid": v(0, 135) * mm, "end": v(-15, 120) * mm});
            skLineSegment(sketch, "E87", {"start": v(-80, 0) * mm, "end": v(80, 0) * mm, "construction": true});
            skLineSegment(sketch, "E88.MirrorCS", {"start": v(15, -108) * mm, "end": v(15, -120) * mm});
            skCircle(sketch, "E89.MirrorC", {"center": v(0, -120) * mm, "radius": 6 * mm});
            skArc(sketch, "E90.MirrorCS", {"start": v(15, -120) * mm, "mid": v(0, -135) * mm, "end": v(-15, -120) * mm});
            skLineSegment(sketch, "E91.MirrorCS", {"start": v(-15, -108) * mm, "end": v(-15, -120) * mm});
            skLineSegment(sketch, "E92.MirrorCS", {"start": v(33, -90) * mm, "end": v(15, -108) * mm});
            skLineSegment(sketch, "E93.MirrorCS", {"start": v(-33, -90) * mm, "end": v(-15, -108) * mm});
            skLineSegment(sketch, "E94.MirrorCS", {"start": v(0, -90) * mm, "end": v(0, -120) * mm, "construction": true});
            skSolve(sketch);
        }
        {
            var Q0;
            Q0 = qSketchRegion(id + "F16", true);
            var Q1;
            Q1=makeQuery(id+"F2.opExtrude","CAP_FACE",FACE,{"disambiguationData":[OSD([sQuery(id+"F0.wireOp",EDGE,"E12"),sQuery(id+"F0.wireOp",EDGE,"E13"),sQuery(id+"F0.wireOp",EDGE,"E14"),sQuery(id+"F0.wireOp",EDGE,"E15"),sQuery(id+"F0.wireOp",EDGE,"E17.filletArc"),sQuery(id+"F0.wireOp",EDGE,"E18.filletArc"),sQuery(id+"F0.wireOp",EDGE,"E19.filletArc"),sQuery(id+"F0.wireOp",EDGE,"E20.filletArc"),sQuery(id+"F0.wireOp",EDGE,"E25.0"),sQuery(id+"F0.wireOp",EDGE,"E25.1"),sQuery(id+"F0.wireOp",EDGE,"E25.2"),sQuery(id+"F0.wireOp",EDGE,"E25.3"),sQuery(id+"F0.wireOp",EDGE,"E25.4"),sQuery(id+"F0.wireOp",EDGE,"E25.5"),sQuery(id+"F0.wireOp",EDGE,"E25.6"),sQuery(id+"F0.wireOp",EDGE,"E25.7")])],"isStart":false});
            extrude(context, id + "F17", {"entities" : qUnion([Q0]), "endBound" : BoundingType.UP_TO_SURFACE, "endBoundEntityFace" : qUnion([Q1]), "depth" : 25 * mm});
        }
    });
